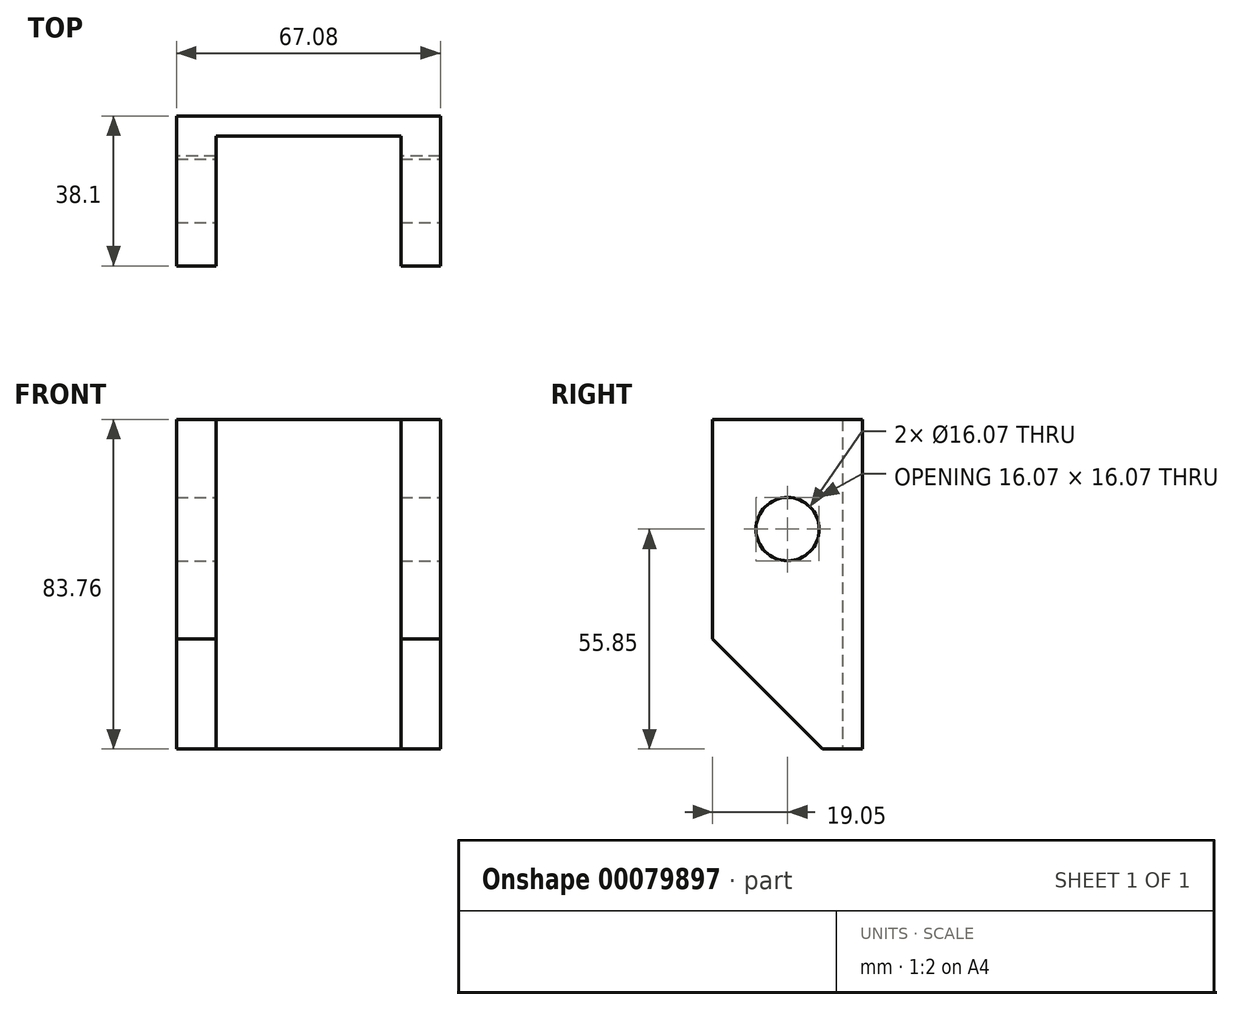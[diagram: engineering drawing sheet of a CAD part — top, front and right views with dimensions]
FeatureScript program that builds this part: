
annotation { "Feature Type Name" : "Feature", "Feature Type Description" : "" }
export const myFeature = defineFeature(function(context is Context, id is Id, definition is map)
    precondition{}
    {
        {
            var Q0;
            Q0=qCreatedBy(makeId("Front.planeOp"),FACE);
            var sketch = newSketch(context, id + "F0", { "sketchPlane" : qUnion([Q0])});
            skLineSegment(sketch, "E0.bottom", {"start": v(33.54, 41.88) * mm, "end": v(-33.54, 41.88) * mm});
            skLineSegment(sketch, "E0.top", {"start": v(33.54, -41.88) * mm, "end": v(-33.54, -41.88) * mm});
            skLineSegment(sketch, "E0.left", {"start": v(33.54, 41.88) * mm, "end": v(33.54, -41.88) * mm});
            skLineSegment(sketch, "E0.right", {"start": v(-33.54, 41.88) * mm, "end": v(-33.54, -41.88) * mm});
            skPoint(sketch, "E0.middle", {"position": v(0, 0) * mm});
            skSolve(sketch);
        }
        {
            var Q0;
            Q0=makeQuery(id+"F0.imprint","IMPRINT",FACE,{"disambiguationData":[TD([[makeQuery(id+"F0.imprint","IMPRINT",EDGE,{"derivedFrom":sQuery(id+"F0.wireOp",EDGE,"E0.bottom")}),1.0]])]});
            extrude(context, id + "F1", {"entities" : qUnion([Q0]), "depth" : 38.1 * mm});
        }
        {
            var Q0;
            Q0=makeQuery(id+"F1.opExtrude","CAP_FACE",FACE,{"disambiguationData":[OSD([sQuery(id+"F0.wireOp",EDGE,"E0.bottom"),sQuery(id+"F0.wireOp",EDGE,"E0.top"),sQuery(id+"F0.wireOp",EDGE,"E0.left"),sQuery(id+"F0.wireOp",EDGE,"E0.right")])],"isStart":false});
            var sketch = newSketch(context, id + "F2", { "sketchPlane" : qUnion([Q0])});
            skLineSegment(sketch, "E1.bottom", {"start": v(23.46, 41.88) * mm, "end": v(-23.46, 41.88) * mm});
            skLineSegment(sketch, "E1.top", {"start": v(23.46, -41.88) * mm, "end": v(-23.46, -41.88) * mm});
            skLineSegment(sketch, "E1.left", {"start": v(23.46, 41.88) * mm, "end": v(23.46, -41.88) * mm});
            skLineSegment(sketch, "E1.right", {"start": v(-23.46, 41.88) * mm, "end": v(-23.46, -41.88) * mm});
            skPoint(sketch, "E1.middle", {"position": v(0, 0) * mm});
            skSolve(sketch);
        }
        {
            var Q0;
            Q0=makeQuery(id+"F2.imprint","IMPRINT",FACE,{"disambiguationData":[TD([[makeQuery(id+"F2.imprint","IMPRINT",EDGE,{"derivedFrom":sQuery(id+"F2.wireOp",EDGE,"E1.bottom")}),1.0]])]});
            extrude(context, id + "F3", {"entities" : qUnion([Q0]), "operationType" : NewBodyOperationType.REMOVE, "oppositeDirection" : true, "depth" : 33.02 * mm});
        }
        {
            var Q0;
            {var subQ0=sQuery(id+"F0.wireOp",EDGE,"E0.left");var subQ1=sQuery(id+"F0.wireOp",EDGE,"E0.top");Q0=makeQuery(id+"F3.boolean.opBoolean","SPLIT",EDGE,{"disambiguationData":[TD([makeQuery(id+"F1.opExtrude","SWEPT_FACE",FACE,{"disambiguationData":[OSD([subQ0])]})])],"derivedFrom":makeQuery(id+"F1.opExtrude","CAP_EDGE",EDGE,{"disambiguationData":[OSD([subQ1])],"isStart":false})});}
            chamfer(context, id + "F4", {"entities" : qUnion([Q0]), "width" : 27.94 * mm, "tangentPropagation" : true});
        }
        {
            var Q0;
            {var subQ0=sQuery(id+"F0.wireOp",EDGE,"E0.right");var subQ1=sQuery(id+"F0.wireOp",EDGE,"E0.top");Q0=makeQuery(id+"F3.boolean.opBoolean","SPLIT",EDGE,{"disambiguationData":[TD([makeQuery(id+"F1.opExtrude","SWEPT_FACE",FACE,{"disambiguationData":[OSD([subQ0])]})])],"derivedFrom":makeQuery(id+"F1.opExtrude","CAP_EDGE",EDGE,{"disambiguationData":[OSD([subQ1])],"isStart":false})});}
            chamfer(context, id + "F5", {"entities" : qUnion([Q0]), "width" : 27.94 * mm, "tangentPropagation" : true});
        }
        {
            var Q0;
            Q0=makeQuery(id+"F1.opExtrude","SWEPT_FACE",FACE,{"disambiguationData":[OSD([sQuery(id+"F0.wireOp",EDGE,"E0.left")])]});
            var sketch = newSketch(context, id + "F6", { "sketchPlane" : qUnion([Q0])});
            skCircle(sketch, "E2", {"center": v(-19.05, 13.97) * mm, "radius": 8.03 * mm});
            skLineSegment(sketch, "E3", {"start": v(-38.1, 13.97) * mm, "end": v(0, 13.97) * mm, "construction": true});
            skSolve(sketch);
        }
        {
            var Q0;
            Q0 = qSketchRegion(id + "F6", true);
            extrude(context, id + "F7", {"entities" : qUnion([Q0]), "operationType" : NewBodyOperationType.REMOVE, "endBound" : BoundingType.THROUGH_ALL, "oppositeDirection" : true, "depth" : 25.4 * mm});
        }
    });
